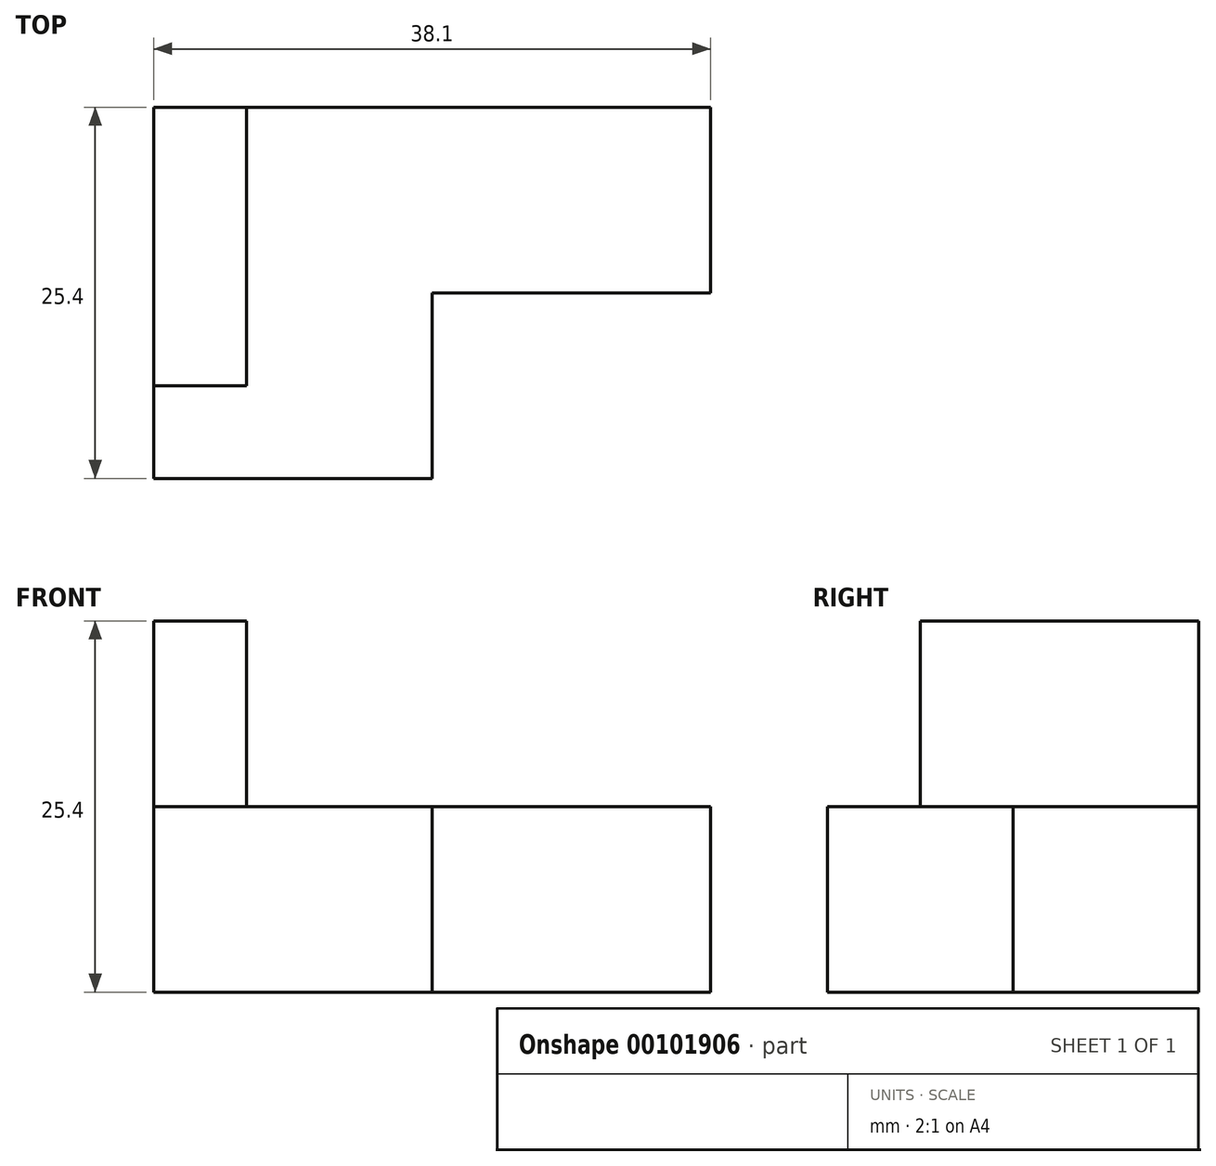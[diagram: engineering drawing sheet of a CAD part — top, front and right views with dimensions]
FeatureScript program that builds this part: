
annotation { "Feature Type Name" : "Feature", "Feature Type Description" : "" }
export const myFeature = defineFeature(function(context is Context, id is Id, definition is map)
    precondition{}
    {
        {
            var Q0;
            Q0=qCreatedBy(makeId("Top.planeOp"),FACE);
            var sketch = newSketch(context, id + "F0", { "sketchPlane" : qUnion([Q0])});
            skLineSegment(sketch, "E0", {"start": v(0, 0) * mm, "end": v(0, -25.4) * mm});
            skLineSegment(sketch, "E1", {"start": v(0, -25.4) * mm, "end": v(19.05, -25.4) * mm});
            skLineSegment(sketch, "E2", {"start": v(19.05, -25.4) * mm, "end": v(19.05, -12.7) * mm});
            skLineSegment(sketch, "E3", {"start": v(19.05, -12.7) * mm, "end": v(38.1, -12.7) * mm});
            skLineSegment(sketch, "E4", {"start": v(38.1, -12.7) * mm, "end": v(38.1, 0) * mm});
            skLineSegment(sketch, "E5", {"start": v(38.1, 0) * mm, "end": v(0, 0) * mm});
            skSolve(sketch);
        }
        {
            var Q0;
            Q0 = qSketchRegion(id + "F0", true);
            extrude(context, id + "F1", {"entities" : qUnion([Q0]), "depth" : 12.7 * mm});
        }
        {
            var Q0;
            Q0=makeQuery(id+"F1.opExtrude","CAP_FACE",FACE,{"disambiguationData":[OSD([sQuery(id+"F0.wireOp",EDGE,"E0"),sQuery(id+"F0.wireOp",EDGE,"E1"),sQuery(id+"F0.wireOp",EDGE,"E2"),sQuery(id+"F0.wireOp",EDGE,"E3"),sQuery(id+"F0.wireOp",EDGE,"E4"),sQuery(id+"F0.wireOp",EDGE,"E5")])],"isStart":false});
            var sketch = newSketch(context, id + "F2", { "sketchPlane" : qUnion([Q0])});
            skLineSegment(sketch, "E6.bottom", {"start": v(0, 0) * mm, "end": v(6.35, 0) * mm});
            skLineSegment(sketch, "E6.top", {"start": v(0, -19.05) * mm, "end": v(6.35, -19.05) * mm});
            skLineSegment(sketch, "E6.left", {"start": v(0, 0) * mm, "end": v(0, -19.05) * mm});
            skLineSegment(sketch, "E6.right", {"start": v(6.35, 0) * mm, "end": v(6.35, -19.05) * mm});
            skSolve(sketch);
        }
        {
            var Q0;
            Q0 = qSketchRegion(id + "F2", true);
            extrude(context, id + "F3", {"entities" : qUnion([Q0]), "operationType" : NewBodyOperationType.ADD, "depth" : 12.7 * mm});
        }
    });
